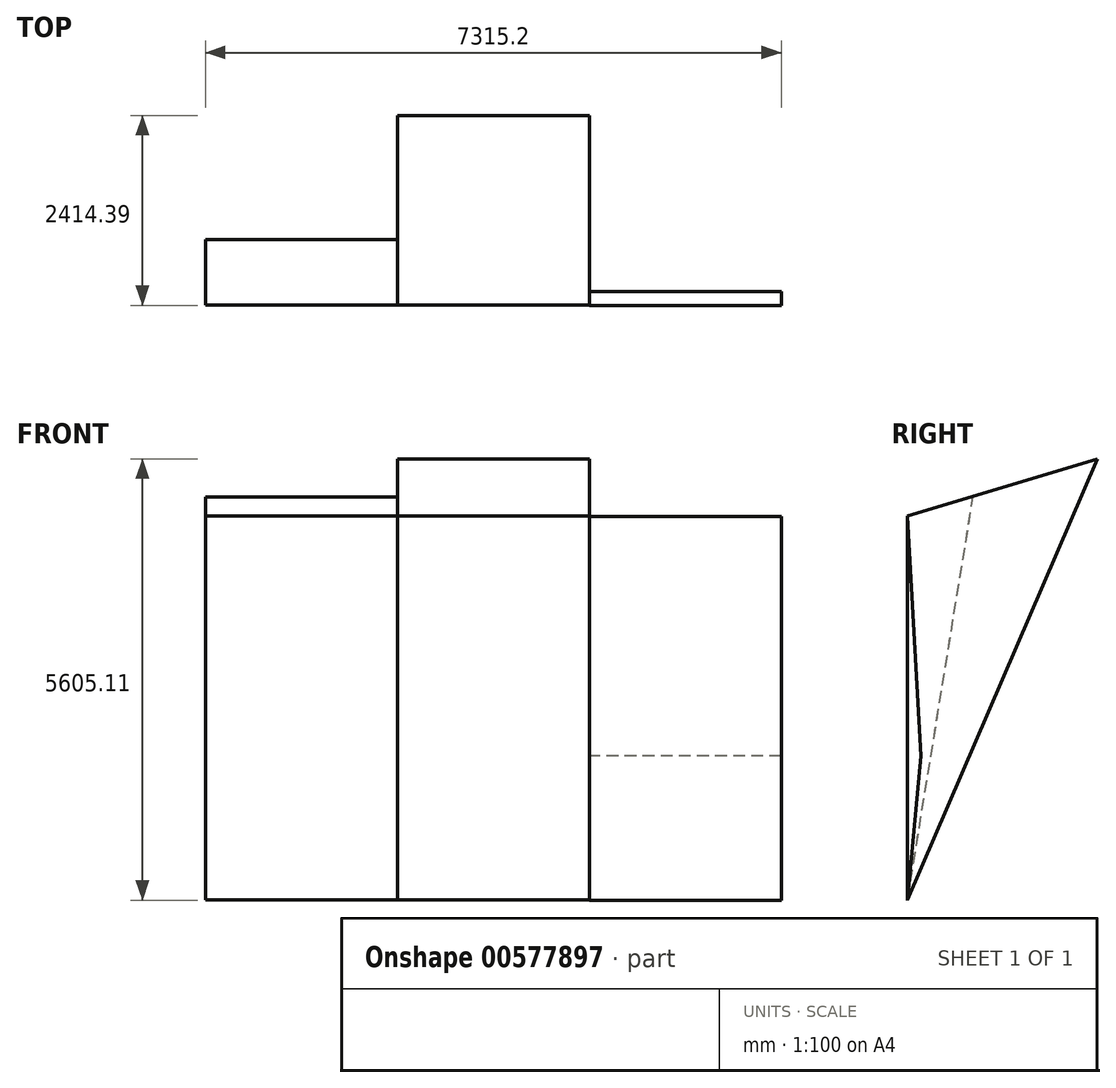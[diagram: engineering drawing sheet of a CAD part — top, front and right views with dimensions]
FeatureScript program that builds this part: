
annotation { "Feature Type Name" : "Feature", "Feature Type Description" : "" }
export const myFeature = defineFeature(function(context is Context, id is Id, definition is map)
    precondition{}
    {
        {
            var Q0;
            Q0=qCreatedBy(makeId("Right.planeOp"),FACE);
            var sketch = newSketch(context, id + "F0", { "sketchPlane" : qUnion([Q0])});
            skLineSegment(sketch, "E0", {"start": v(-53.92, -76.25) * mm, "end": v(-53.92, 4800.55) * mm});
            skLineSegment(sketch, "E1", {"start": v(-53.92, 4800.55) * mm, "end": v(2994.08, 4800.55) * mm});
            skLineSegment(sketch, "E2", {"start": v(2994.08, 4800.55) * mm, "end": v(2994.08, 5714.95) * mm});
            skLineSegment(sketch, "E3", {"start": v(2994.08, 5714.95) * mm, "end": v(-53.92, 4800.55) * mm});
            skLineSegment(sketch, "E4", {"start": v(-53.92, -76.25) * mm, "end": v(2355.51, 5523.38) * mm});
            skSolve(sketch);
        }
        {
            var Q0;
            {var subQ0=sQuery(id+"F0.wireOp",EDGE,"E3");var subQ3=sQuery(id+"F0.wireOp",EDGE,"E4");var subQ5=makeQuery(id+"F0.imprint","INTERSECT",VERTEX,{"derivedFrom":[subQ0,subQ3]});Q0=makeQuery(id+"F0.imprint","IMPRINT",FACE,{"disambiguationData":[TD([[makeQuery(id+"F0.imprint","IMPRINT",EDGE,{"disambiguationData":[TD([[subQ5,1.0]])],"derivedFrom":subQ3}),1.0]])]});}
            var Q1;
            {var subQ0=sQuery(id+"F0.wireOp",EDGE,"E0");Q1=makeQuery(id+"F0.imprint","IMPRINT",FACE,{"disambiguationData":[TD([[makeQuery(id+"F0.imprint","IMPRINT",EDGE,{"derivedFrom":subQ0}),-1.0]])]});}
            extrude(context, id + "F1", {"entities" : qUnion([Q0, Q1]), "depth" : 2438.4 * mm, "offsetDistance" : 25.4 * mm});
        }
        {
            var Q0;
            Q0=qCreatedBy(makeId("Right.planeOp"),FACE);
            var sketch = newSketch(context, id + "F2", { "sketchPlane" : qUnion([Q0])});
            skLineSegment(sketch, "E5", {"start": v(-54.71, -76.77) * mm, "end": v(-54.71, 4800.03) * mm});
            skLineSegment(sketch, "E6", {"start": v(-54.71, -76.77) * mm, "end": v(777.97, 5037.49) * mm});
            skLineSegment(sketch, "E7", {"start": v(777.97, 5037.49) * mm, "end": v(-54.71, 4800.03) * mm});
            skSolve(sketch);
        }
        {
            var Q0;
            Q0 = qSketchRegion(id + "F2", true);
            extrude(context, id + "F3", {"entities" : qUnion([Q0]), "operationType" : NewBodyOperationType.ADD, "oppositeDirection" : true, "depth" : 2438.4 * mm, "offsetDistance" : 25.4 * mm});
        }
        {
            var Q0;
            Q0=qCreatedBy(makeId("Right.planeOp"),FACE);
            var sketch = newSketch(context, id + "F4", { "sketchPlane" : qUnion([Q0])});
            skLineSegment(sketch, "E8", {"start": v(-58.88, -81.73) * mm, "end": v(-58.88, 4795.07) * mm});
            skLineSegment(sketch, "E9", {"start": v(-58.88, 4795.07) * mm, "end": v(117.18, 1752.16) * mm});
            skLineSegment(sketch, "E10", {"start": v(117.18, 1752.16) * mm, "end": v(-58.88, -81.73) * mm});
            skSolve(sketch);
        }
        {
            var Q0;
            Q0 = qSketchRegion(id + "F4", true);
            extrude(context, id + "F5", {"entities" : qUnion([Q0]), "operationType" : NewBodyOperationType.ADD, "depth" : 4876.8 * mm, "offsetDistance" : 25.4 * mm, "hasSecondDirection" : true, "secondDirectionOppositeDirection" : false, "secondDirectionDepth" : 2438.4 * mm});
        }
    });
